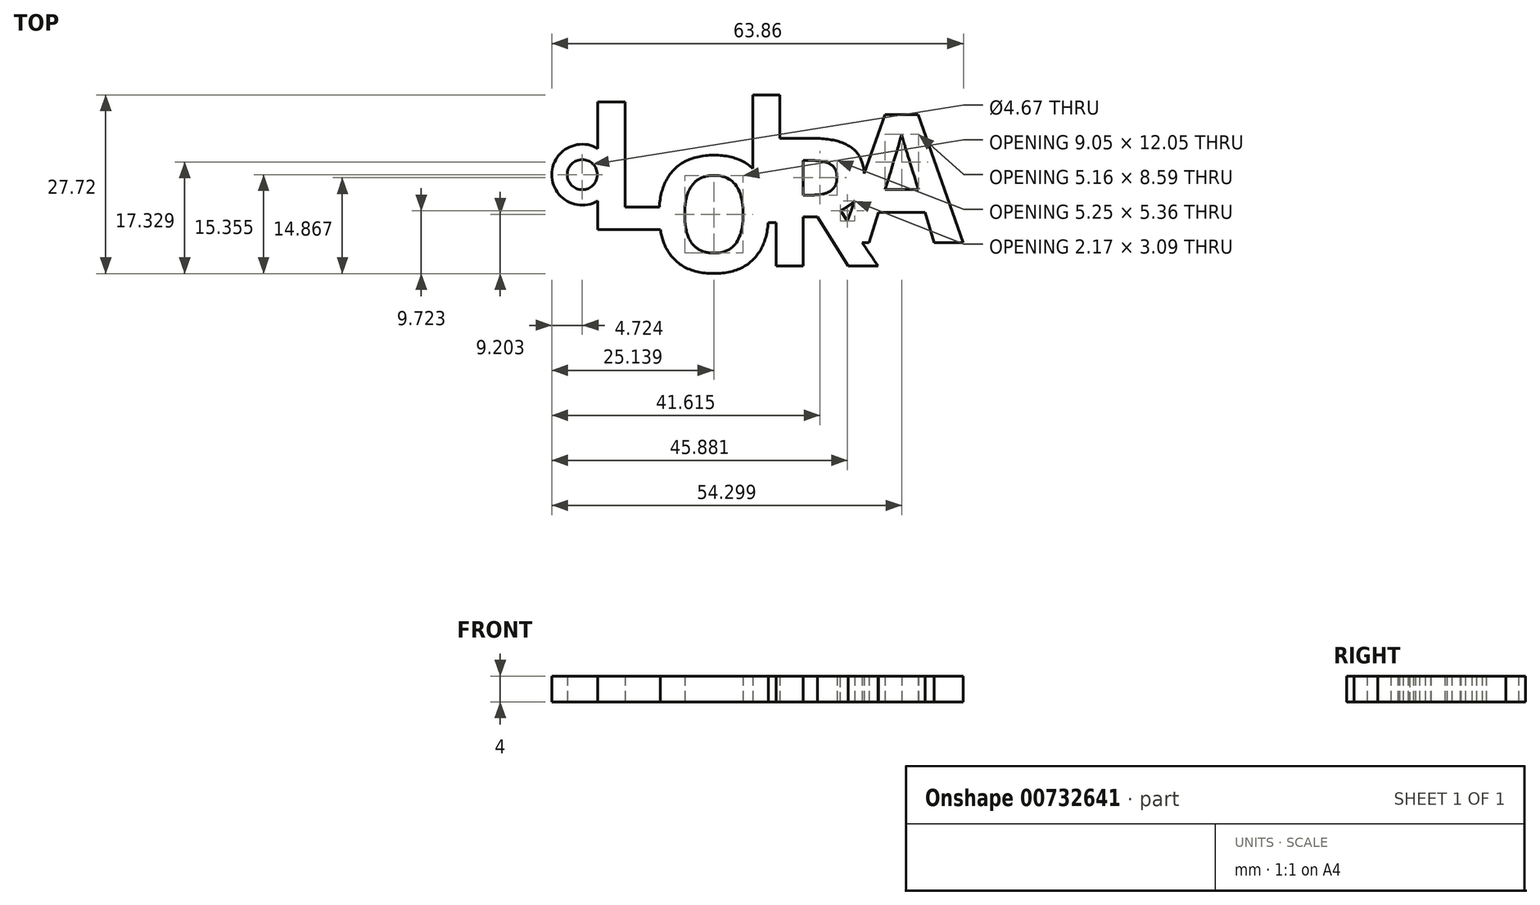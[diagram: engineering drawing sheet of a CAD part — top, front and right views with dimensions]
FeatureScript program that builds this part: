
annotation { "Feature Type Name" : "Feature", "Feature Type Description" : "" }
export const myFeature = defineFeature(function(context is Context, id is Id, definition is map)
    precondition{}
    {
        {
            var Q0;
            Q0=qCreatedBy(makeId("Top.planeOp"),FACE);
            var sketch = newSketch(context, id + "F0", { "sketchPlane" : qUnion([Q0])});
            skText(sketch, "E0", { "text": "L", "fontName": "OpenSans-Bold.ttf"});
            skText(sketch, "E1", { "text": "O", "fontName": "OpenSans-Bold.ttf"});
            skText(sketch, "E2", { "text": "I", "fontName": "OpenSans-Bold.ttf"});
            skText(sketch, "E3", { "text": "R", "fontName": "OpenSans-Bold.ttf"});
            skText(sketch, "E4", { "text": "A", "fontName": "OpenSans-Bold.ttf"});
            const initialGuessF0  = {"E0": [-0.03978, 0.01818, 1, 0, 0.02], "E1": [-0.02923, 0.01159, 1, 0, 0.018], "E2": [-0.01572, 0.01923, 1, 0, 0.02], "E3": [-0.01213, 0.0125, 1, 0, 0.02], "E4": [0.00027, 0.01613, 1, 0, 0.02]};
            skSetInitialGuess(sketch, initialGuessF0);
            skSolve(sketch);
        }
        {
            var Q0;
            Q0 = qSketchRegion(id + "F0", true);
            extrude(context, id + "F1", {"entities" : qUnion([Q0]), "depth" : 4 * mm, "offsetDistance" : 25 * mm});
        }
        {
            var Q0;
            Q0=qCreatedBy(makeId("Top.planeOp"),FACE);
            var sketch = newSketch(context, id + "F2", { "sketchPlane" : qUnion([Q0])});
            skCircle(sketch, "E5", {"center": v(-39.7, 26.7) * mm, "radius": 4.73 * mm});
            skCircle(sketch, "E6", {"center": v(-39.7, 26.7) * mm, "radius": 2.33 * mm});
            skSolve(sketch);
        }
        {
            var Q0;
            Q0 = qSketchRegion(id + "F2", true);
            extrude(context, id + "F3", {"entities" : qUnion([Q0]), "operationType" : NewBodyOperationType.ADD, "depth" : 4 * mm, "offsetDistance" : 25 * mm});
        }
    });
